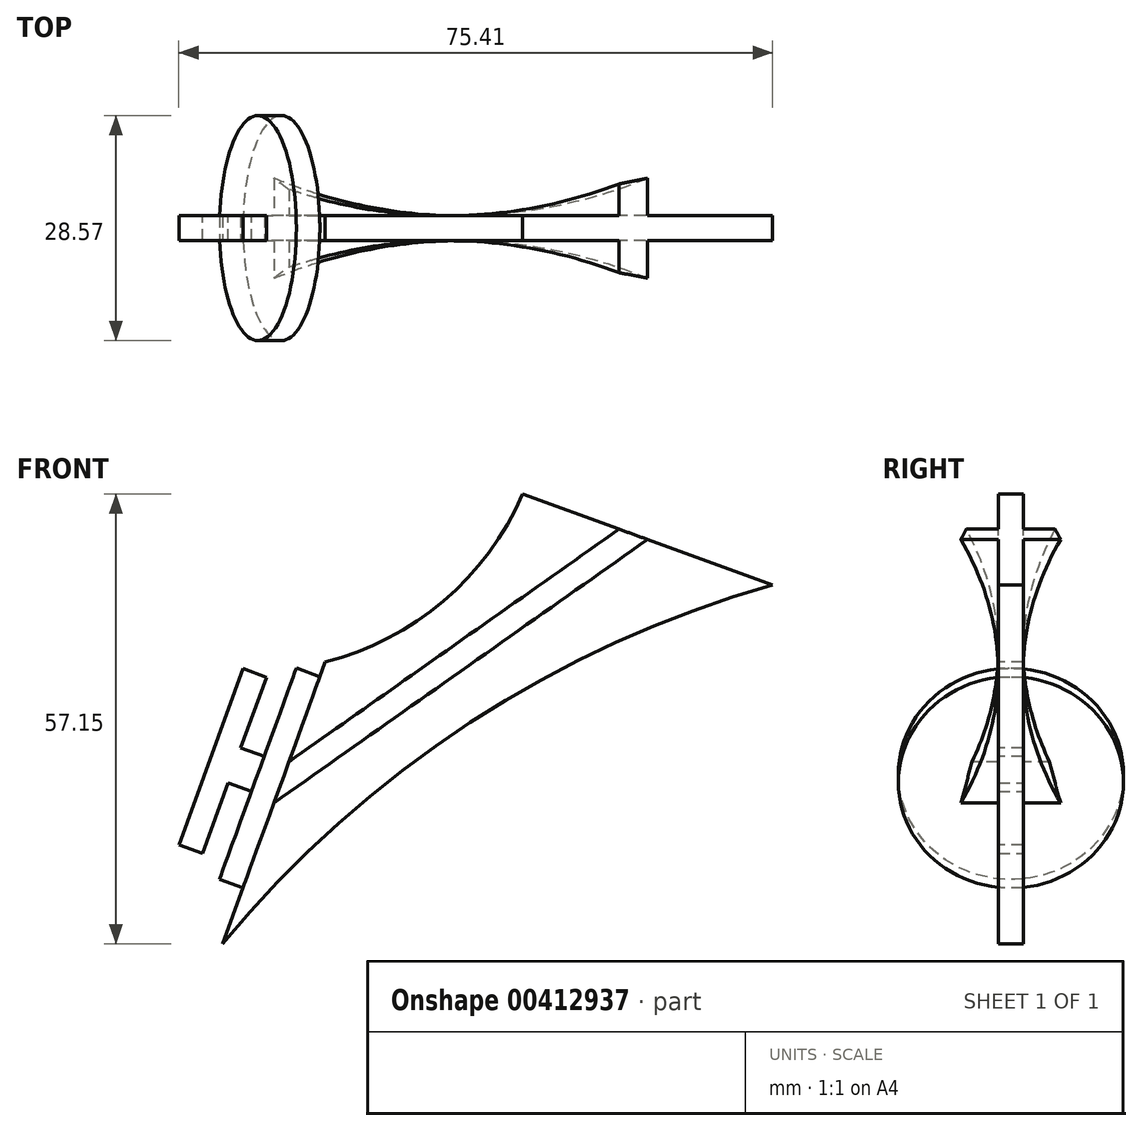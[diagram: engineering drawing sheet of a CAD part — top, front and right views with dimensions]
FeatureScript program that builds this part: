
annotation { "Feature Type Name" : "Feature", "Feature Type Description" : "" }
export const myFeature = defineFeature(function(context is Context, id is Id, definition is map)
    precondition{}
    {
        {
            var Q0;
            Q0=qCreatedBy(makeId("Front.planeOp"),FACE);
            var sketch = newSketch(context, id + "F0", { "sketchPlane" : qUnion([Q0])});
            skLineSegment(sketch, "E0", {"start": v(0, 0) * mm, "end": v(13.03, 35.8) * mm});
            skLineSegment(sketch, "E1", {"start": v(38.1, 57.15) * mm, "end": v(69.85, 45.6) * mm});
            skArc(sketch, "E2", {"start": v(13.03, 35.8) * mm, "mid": v(28.05, 43.56) * mm, "end": v(38.1, 57.15) * mm});
            skArc(sketch, "E3", {"start": v(69.85, 45.6) * mm, "mid": v(31.45, 28.12) * mm, "end": v(0, 0) * mm});
            skLineSegment(sketch, "E4", {"start": v(53.97, 51.37) * mm, "end": v(6.52, 17.9) * mm});
            skLineSegment(sketch, "E5.0", {"start": v(50.34, 52.7) * mm, "end": v(8.42, 23.13) * mm});
            skSolve(sketch);
        }
        {
            var Q0;
            {var subQ0=sQuery(id+"F0.wireOp",EDGE,"E3");Q0=makeQuery(id+"F0.imprint","IMPRINT",FACE,{"disambiguationData":[TD([[makeQuery(id+"F0.imprint","IMPRINT",EDGE,{"derivedFrom":subQ0}),-1.0]])]});}
            var Q1;
            {var subQ0=sQuery(id+"F0.wireOp",EDGE,"E2");Q1=makeQuery(id+"F0.imprint","IMPRINT",FACE,{"disambiguationData":[TD([[makeQuery(id+"F0.imprint","IMPRINT",EDGE,{"derivedFrom":subQ0}),-1.0]])]});}
            extrude(context, id + "F1", {"entities" : qUnion([Q0, Q1]), "oppositeDirection" : true, "depth" : 1.59 * mm, "hasSecondDirection" : true, "secondDirectionOppositeDirection" : false, "secondDirectionDepth" : 1.59 * mm});
        }
        {
            var Q0;
            {var subQ0=sQuery(id+"F0.wireOp",EDGE,"E4");Q0=makeQuery(id+"F0.imprint","IMPRINT",FACE,{"disambiguationData":[TD([[makeQuery(id+"F0.imprint","IMPRINT",EDGE,{"derivedFrom":subQ0}),-1.0]])]});}
            extrude(context, id + "F2", {"entities" : qUnion([Q0]), "oppositeDirection" : true, "depth" : 6.35 * mm, "hasSecondDirection" : true, "secondDirectionOppositeDirection" : false, "secondDirectionDepth" : 6.35 * mm});
        }
        {
            var Q0;
            Q0=makeQuery(id+"F2.opExtrude","SWEPT_FACE",FACE,{"disambiguationData":[OSD([sQuery(id+"F0.wireOp",EDGE,"E4")])]});
            var sketch = newSketch(context, id + "F3", { "sketchPlane" : qUnion([Q0])});
            skArc(sketch, "E6", {"start": v(15.64, 6.35) * mm, "mid": v(44.68, 1.59) * mm, "end": v(73.72, 6.35) * mm});
            skLineSegment(sketch, "E7", {"start": v(73.72, 6.35) * mm, "end": v(15.64, 6.35) * mm});
            skLineSegment(sketch, "E8", {"start": v(44.68, 6.35) * mm, "end": v(44.68, 1.59) * mm, "construction": true});
            skPoint(sketch, "E8.endSnap0", {"position": v(44.68, 1.59) * mm});
            skLineSegment(sketch, "E9", {"start": v(73.72, -6.35) * mm, "end": v(15.64, -6.35) * mm});
            skArc(sketch, "E10", {"start": v(73.72, -6.35) * mm, "mid": v(44.68, -1.59) * mm, "end": v(15.64, -6.35) * mm});
            skSolve(sketch);
        }
        {
            var Q0;
            Q0=makeQuery(id+"F3.imprint","IMPRINT",FACE,{"disambiguationData":[TD([[makeQuery(id+"F3.imprint","IMPRINT",EDGE,{"derivedFrom":sQuery(id+"F3.wireOp",EDGE,"E6")}),1.0]])]});
            var Q1;
            Q1=makeQuery(id+"F3.imprint","IMPRINT",FACE,{"disambiguationData":[TD([[makeQuery(id+"F3.imprint","IMPRINT",EDGE,{"derivedFrom":sQuery(id+"F3.wireOp",EDGE,"E9")}),-1.0]])]});
            extrude(context, id + "F4", {"entities" : qUnion([Q0, Q1]), "operationType" : NewBodyOperationType.REMOVE, "oppositeDirection" : true, "depth" : 3.17 * mm});
        }
        {
            var Q0;
            Q0=makeQuery(id+"F1.opExtrude","SWEPT_BODY",BODY,{"disambiguationData":[OSD([sQuery(id+"F0.wireOp",EDGE,"E0"),sQuery(id+"F0.wireOp",EDGE,"E1"),sQuery(id+"F0.wireOp",EDGE,"E2"),sQuery(id+"F0.wireOp",EDGE,"E5.0")])]});
            var Q1;
            Q1=makeQuery(id+"F2.opExtrude","SWEPT_BODY",BODY,{"disambiguationData":[OSD([sQuery(id+"F0.wireOp",EDGE,"E0"),sQuery(id+"F0.wireOp",EDGE,"E1"),sQuery(id+"F0.wireOp",EDGE,"E4"),sQuery(id+"F0.wireOp",EDGE,"E5.0")])]});
            var Q2;
            Q2=makeQuery(id+"F1.opExtrude","SWEPT_BODY",BODY,{"disambiguationData":[OSD([sQuery(id+"F0.wireOp",EDGE,"E0"),sQuery(id+"F0.wireOp",EDGE,"E1"),sQuery(id+"F0.wireOp",EDGE,"E3"),sQuery(id+"F0.wireOp",EDGE,"E4")])]});
            booleanBodies(context, id + "F5", {"operationType" : BooleanOperationType.UNION, "tools" : qUnion([Q0, Q1, Q2])});
        }
        {
            var Q0;
            {var subQ0=sQuery(id+"F0.wireOp",EDGE,"E0");Q0=makeQuery(id+"F5.opBoolean","MERGE",FACE,{"derivedFrom":[makeQuery(id+"F1.opExtrude","SWEPT_FACE",FACE,{"disambiguationData":[OSD([subQ0]),TDD([makeQuery(id+"F0.imprint","IMPRINT",EDGE,{"disambiguationData":[TD([[makeQuery(id+"F0.imprint","INTERSECT",VERTEX,{"derivedFrom":[subQ0,sQuery(id+"F0.wireOp",EDGE,"E3")]}),-1.0]])],"derivedFrom":subQ0})])]}),makeQuery(id+"F1.opExtrude","SWEPT_FACE",FACE,{"disambiguationData":[OSD([subQ0]),TDD([makeQuery(id+"F0.imprint","IMPRINT",EDGE,{"disambiguationData":[TD([[makeQuery(id+"F0.imprint","INTERSECT",VERTEX,{"derivedFrom":[subQ0,sQuery(id+"F0.wireOp",EDGE,"E2")]}),1.0]])],"derivedFrom":subQ0})])]}),makeQuery(id+"F2.opExtrude","SWEPT_FACE",FACE,{"disambiguationData":[OSD([subQ0])]})]});}
            var sketch = newSketch(context, id + "F6", { "sketchPlane" : qUnion([Q0])});
            skLineSegment(sketch, "E11", {"start": v(-1.59, 24.61) * mm, "end": v(-1.59, 19.05) * mm, "construction": true});
            skLineSegment(sketch, "E12", {"start": v(-1.59, 21.83) * mm, "end": v(5.61, 21.83) * mm, "construction": true});
            skLineSegment(sketch, "E13.bottom", {"start": v(-1.59, 33.74) * mm, "end": v(1.59, 33.74) * mm});
            skLineSegment(sketch, "E13.top", {"start": v(-1.59, 9.92) * mm, "end": v(1.59, 9.92) * mm});
            skLineSegment(sketch, "E13.left", {"start": v(-1.59, 33.74) * mm, "end": v(-1.59, 9.92) * mm});
            skLineSegment(sketch, "E13.right", {"start": v(1.59, 33.74) * mm, "end": v(1.59, 9.92) * mm});
            skLineSegment(sketch, "E14", {"start": v(-1.59, 21.83) * mm, "end": v(-8.52, 21.83) * mm, "construction": true});
            skSolve(sketch);
        }
        {
            var Q0;
            {var subQ20=sQuery(id+"F6.wireOp",EDGE,"E13.bottom");Q0=makeQuery(id+"F6.imprint","IMPRINT",FACE,{"disambiguationData":[TD([[makeQuery(id+"F6.imprint","IMPRINT",EDGE,{"derivedFrom":subQ20}),-1.0]])]});}
            extrude(context, id + "F7", {"entities" : qUnion([Q0]), "operationType" : NewBodyOperationType.ADD, "depth" : 9.52 * mm});
        }
        {
            var Q0;
            {var subQ1=sQuery(id+"F0.wireOp",EDGE,"E2");var subQ3=sQuery(id+"F0.wireOp",EDGE,"E0");var subQ5=sQuery(id+"F0.wireOp",EDGE,"E3");Q0=makeQuery(id+"F7.boolean.opBoolean","SPLIT",FACE,{"disambiguationData":[TD([makeQuery(id+"F1.opExtrude","SWEPT_FACE",FACE,{"disambiguationData":[OSD([subQ1])]})])],"derivedFrom":makeQuery(id+"F5.opBoolean","MERGE",FACE,{"derivedFrom":[makeQuery(id+"F1.opExtrude","SWEPT_FACE",FACE,{"disambiguationData":[OSD([subQ3]),TDD([makeQuery(id+"F0.imprint","IMPRINT",EDGE,{"disambiguationData":[TD([[makeQuery(id+"F0.imprint","INTERSECT",VERTEX,{"derivedFrom":[subQ3,subQ5]}),-1.0]])],"derivedFrom":subQ3})])]}),makeQuery(id+"F1.opExtrude","SWEPT_FACE",FACE,{"disambiguationData":[OSD([subQ3]),TDD([makeQuery(id+"F0.imprint","IMPRINT",EDGE,{"disambiguationData":[TD([[makeQuery(id+"F0.imprint","INTERSECT",VERTEX,{"derivedFrom":[subQ3,subQ1]}),1.0]])],"derivedFrom":subQ3})])]}),makeQuery(id+"F2.opExtrude","SWEPT_FACE",FACE,{"disambiguationData":[OSD([subQ3])]})]})});}
            var sketch = newSketch(context, id + "F8", { "sketchPlane" : qUnion([Q0])});
            skLineSegment(sketch, "E15.bottom", {"start": v(-1.59, 33.74) * mm, "end": v(1.59, 33.74) * mm});
            skLineSegment(sketch, "E15.top", {"start": v(-1.59, 24.21) * mm, "end": v(1.59, 24.21) * mm});
            skLineSegment(sketch, "E15.left", {"start": v(-1.59, 33.74) * mm, "end": v(-1.59, 24.21) * mm});
            skLineSegment(sketch, "E15.right", {"start": v(1.59, 33.74) * mm, "end": v(1.59, 24.21) * mm});
            skLineSegment(sketch, "E16.bottom", {"start": v(1.59, 9.92) * mm, "end": v(-1.59, 9.92) * mm});
            skLineSegment(sketch, "E16.top", {"start": v(1.59, 19.45) * mm, "end": v(-1.59, 19.45) * mm});
            skLineSegment(sketch, "E16.left", {"start": v(1.59, 9.92) * mm, "end": v(1.59, 19.45) * mm});
            skLineSegment(sketch, "E16.right", {"start": v(-1.59, 9.92) * mm, "end": v(-1.59, 19.45) * mm});
            skSolve(sketch);
        }
        {
            var Q0;
            Q0=makeQuery(id+"F8.imprint","IMPRINT",FACE,{"disambiguationData":[TD([[makeQuery(id+"F8.imprint","IMPRINT",EDGE,{"derivedFrom":sQuery(id+"F8.wireOp",EDGE,"E15.bottom")}),-1.0]])]});
            var Q1;
            Q1=makeQuery(id+"F8.imprint","IMPRINT",FACE,{"disambiguationData":[TD([[makeQuery(id+"F8.imprint","IMPRINT",EDGE,{"derivedFrom":sQuery(id+"F8.wireOp",EDGE,"E16.bottom")}),-1.0]])]});
            extrude(context, id + "F9", {"entities" : qUnion([Q0, Q1]), "operationType" : NewBodyOperationType.REMOVE, "depth" : 6.35 * mm});
        }
        {
            var Q0;
            {var subQ20=sQuery(id+"F6.wireOp",EDGE,"E13.bottom");Q0=makeQuery(id+"F6.imprint","IMPRINT",FACE,{"disambiguationData":[TD([[makeQuery(id+"F6.imprint","IMPRINT",EDGE,{"derivedFrom":subQ20}),-1.0]])]});}
            var sketch = newSketch(context, id + "F10", { "sketchPlane" : qUnion([Q0])});
            skCircle(sketch, "E17", {"center": v(-0.02, 21.83) * mm, "radius": 14.29 * mm});
            skLineSegment(sketch, "E18", {"start": v(-0.02, 21.83) * mm, "end": v(-0.02, 0) * mm, "construction": true});
            skLineSegment(sketch, "E19", {"start": v(-1.61, 0) * mm, "end": v(1.56, 0) * mm, "construction": true});
            skLineSegment(sketch, "E20", {"start": v(-1.59, 33.74) * mm, "end": v(-1.59, 9.92) * mm, "construction": true});
            skLineSegment(sketch, "E21", {"start": v(-1.59, 21.83) * mm, "end": v(1.59, 21.83) * mm, "construction": true});
            skSolve(sketch);
        }
        {
            var Q0;
            {var subQ20=sQuery(id+"F6.wireOp",EDGE,"E13.bottom");Q0=makeQuery(id+"F10.imprint","IMPRINT",FACE,{"disambiguationData":[TD([[makeQuery(id+"F10.imprint","IMPRINT",EDGE,{"derivedFrom":makeQuery(id+"F6.imprint","IMPRINT",EDGE,{"derivedFrom":subQ20})}),-1.0]])]});}
            var Q1;
            Q1=makeQuery(id+"F10.imprint","IMPRINT",FACE,{"disambiguationData":[TD([[makeQuery(id+"F10.imprint","IMPRINT",EDGE,{"derivedFrom":sQuery(id+"F10.wireOp",EDGE,"E17")}),1.0]])]});
            extrude(context, id + "F11", {"entities" : qUnion([Q0, Q1]), "operationType" : NewBodyOperationType.ADD, "depth" : 3.17 * mm});
        }
    });
